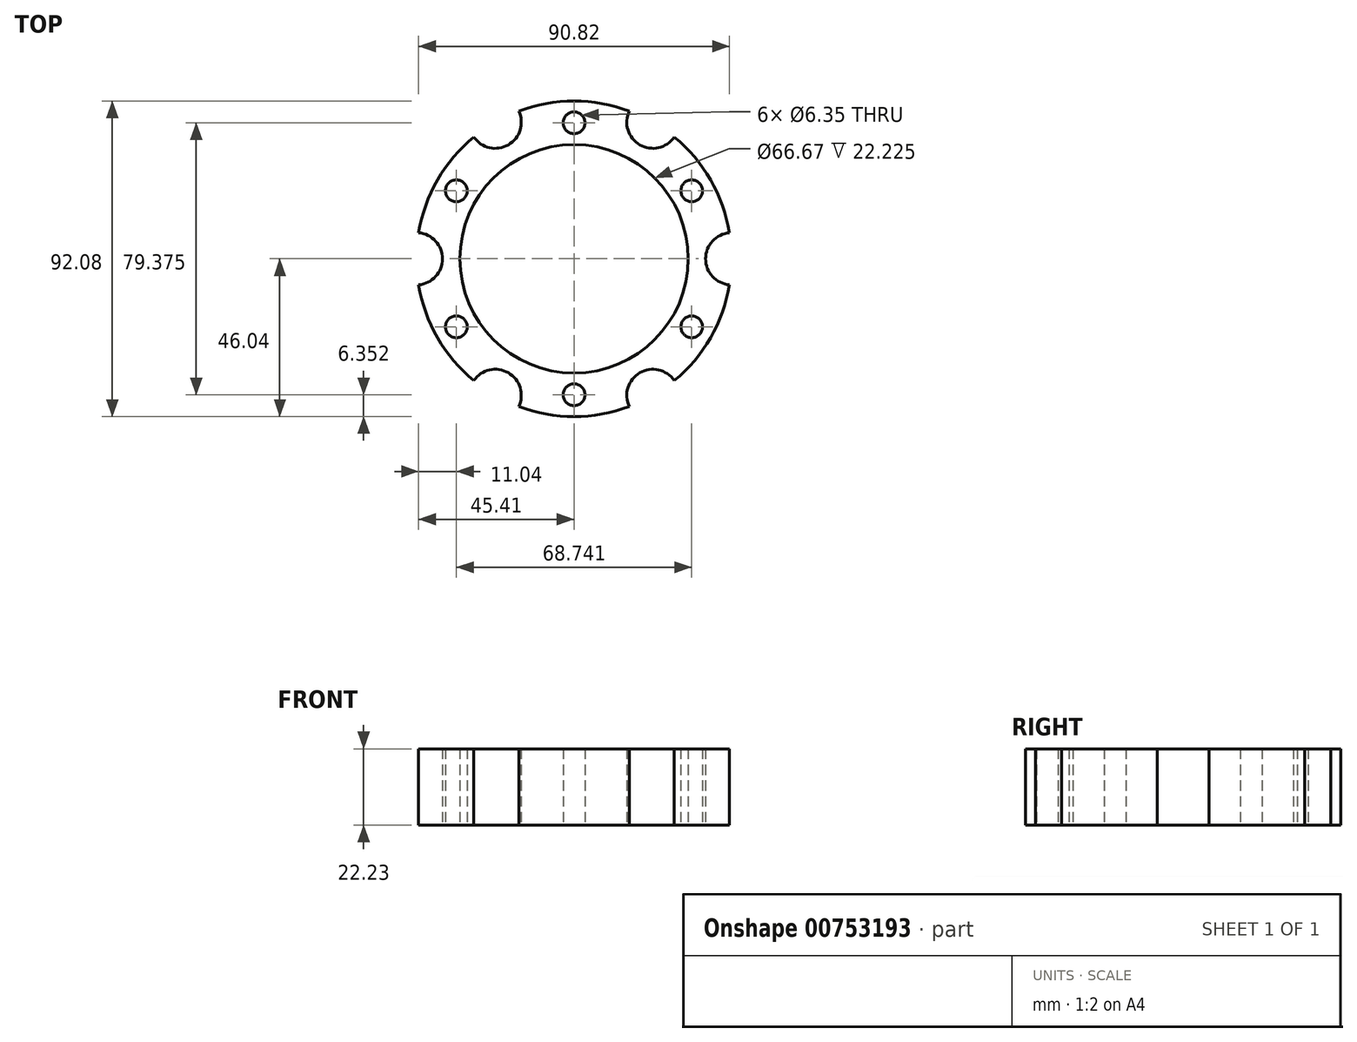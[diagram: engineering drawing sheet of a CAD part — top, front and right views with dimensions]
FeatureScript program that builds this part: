
annotation { "Feature Type Name" : "Feature", "Feature Type Description" : "" }
export const myFeature = defineFeature(function(context is Context, id is Id, definition is map)
    precondition{}
    {
        {
            var Q0;
            Q0=qCreatedBy(makeId("Top.planeOp"),FACE);
            var sketch = newSketch(context, id + "F0", { "sketchPlane" : qUnion([Q0])});
            skCircle(sketch, "E0", {"center": v(0, 0) * mm, "radius": 33.34 * mm});
            skCircle(sketch, "E1", {"center": v(0, 0) * mm, "radius": 46.04 * mm});
            skCircle(sketch, "E2", {"center": v(-46.04, 0) * mm, "radius": 7.62 * mm});
            skCircle(sketch, "E3.1.0", {"center": v(-23.02, -39.87) * mm, "radius": 7.62 * mm});
            skCircle(sketch, "E3.2.0", {"center": v(23.02, -39.87) * mm, "radius": 7.62 * mm});
            skCircle(sketch, "E3.3.0", {"center": v(46.04, 0) * mm, "radius": 7.62 * mm});
            skCircle(sketch, "E3.4.0", {"center": v(23.02, 39.87) * mm, "radius": 7.62 * mm});
            skCircle(sketch, "E3.5.0", {"center": v(-23.02, 39.87) * mm, "radius": 7.62 * mm});
            skLineSegment(sketch, "E4", {"start": v(0, 33.34) * mm, "end": v(0, 46.04) * mm, "construction": true});
            skCircle(sketch, "E5", {"center": v(0, 39.69) * mm, "radius": 3.18 * mm});
            skCircle(sketch, "E6.1.0", {"center": v(-34.37, 19.84) * mm, "radius": 3.18 * mm});
            skCircle(sketch, "E6.2.0", {"center": v(-34.37, -19.84) * mm, "radius": 3.18 * mm});
            skCircle(sketch, "E6.3.0", {"center": v(0, -39.69) * mm, "radius": 3.18 * mm});
            skCircle(sketch, "E6.4.0", {"center": v(34.37, -19.84) * mm, "radius": 3.18 * mm});
            skCircle(sketch, "E6.5.0", {"center": v(34.37, 19.84) * mm, "radius": 3.18 * mm});
            skCircle(sketch, "E7.0", {"center": v(0, 0) * mm, "radius": 26.99 * mm});
            skCircle(sketch, "E8.0", {"center": v(0, 0) * mm, "radius": 14.29 * mm});
            skCircle(sketch, "E9", {"center": v(-20.64, 0) * mm, "radius": 3.18 * mm});
            skLineSegment(sketch, "E10", {"start": v(-26.99, 0) * mm, "end": v(-14.29, 0) * mm, "construction": true});
            skCircle(sketch, "E11.1.0", {"center": v(10.32, -17.87) * mm, "radius": 3.18 * mm});
            skCircle(sketch, "E11.2.0", {"center": v(10.32, 17.87) * mm, "radius": 3.18 * mm});
            skSolve(sketch);
        }
        {
            var Q0;
            Q0=makeQuery(id+"F0.imprint","IMPRINT",FACE,{"disambiguationData":[TD([[makeQuery(id+"F0.imprint","IMPRINT",EDGE,{"derivedFrom":sQuery(id+"F0.wireOp",EDGE,"E0")}),-1.0]])]});
            extrude(context, id + "F1", {"entities" : qUnion([Q0]), "depth" : 22.22 * mm, "offsetDistance" : 25.4 * mm});
        }
    });
